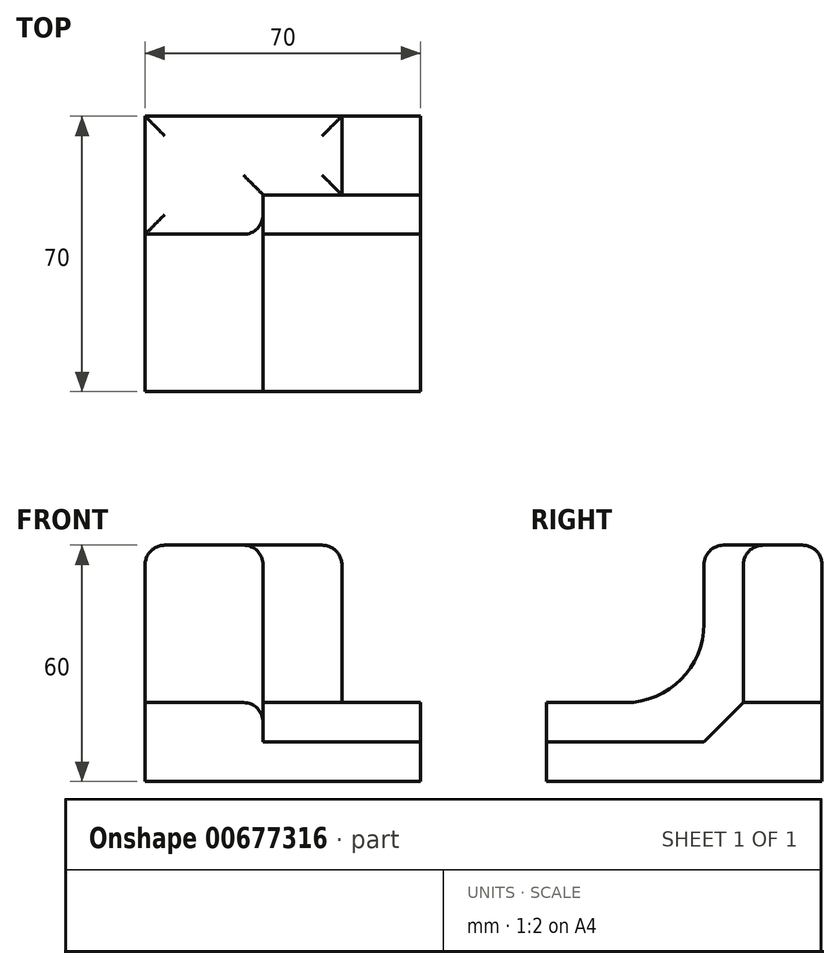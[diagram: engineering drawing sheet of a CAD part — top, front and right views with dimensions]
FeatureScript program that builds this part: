
annotation { "Feature Type Name" : "Feature", "Feature Type Description" : "" }
export const myFeature = defineFeature(function(context is Context, id is Id, definition is map)
    precondition{}
    {
        {
            var Q0;
            Q0=qCreatedBy(makeId("Top.planeOp"),FACE);
            var sketch = newSketch(context, id + "F0", { "sketchPlane" : qUnion([Q0])});
            skLineSegment(sketch, "E0.bottom", {"start": v(0, 0) * mm, "end": v(70, 0) * mm});
            skLineSegment(sketch, "E0.top", {"start": v(0, 70) * mm, "end": v(70, 70) * mm});
            skLineSegment(sketch, "E0.left", {"start": v(0, 0) * mm, "end": v(0, 70) * mm});
            skLineSegment(sketch, "E0.right", {"start": v(70, 0) * mm, "end": v(70, 70) * mm});
            skSolve(sketch);
        }
        {
            var Q0;
            Q0 = qSketchRegion(id + "F0", true);
            extrude(context, id + "F1", {"entities" : qUnion([Q0]), "depth" : 60 * mm, "offsetDistance" : 25 * mm});
        }
        {
            var Q0;
            Q0=makeQuery(id+"F1.opExtrude","SWEPT_FACE",FACE,{"disambiguationData":[OSD([sQuery(id+"F0.wireOp",EDGE,"E0.right")])]});
            var sketch = newSketch(context, id + "F2", { "sketchPlane" : qUnion([Q0])});
            skLineSegment(sketch, "E1", {"start": v(0, 60) * mm, "end": v(40, 60) * mm});
            skLineSegment(sketch, "E2", {"start": v(40, 60) * mm, "end": v(40, 40) * mm});
            skLineSegment(sketch, "E3", {"start": v(20, 20) * mm, "end": v(0, 20) * mm});
            skLineSegment(sketch, "E4", {"start": v(0, 20) * mm, "end": v(0, 60) * mm});
            skPoint(sketch, "E5.visualSharp", {"position": v(40, 20) * mm});
            skArc(sketch, "E5.filletArc", {"start": v(20, 20) * mm, "mid": v(34.14, 25.86) * mm, "end": v(40, 40) * mm});
            skSolve(sketch);
        }
        {
            var Q0;
            Q0 = qSketchRegion(id + "F2", true);
            extrude(context, id + "F3", {"entities" : qUnion([Q0]), "operationType" : NewBodyOperationType.REMOVE, "endBound" : BoundingType.THROUGH_ALL, "oppositeDirection" : true, "depth" : 25 * mm, "offsetDistance" : 25 * mm});
        }
        {
            var Q0;
            Q0=makeQuery(id+"F1.opExtrude","SWEPT_FACE",FACE,{"disambiguationData":[OSD([sQuery(id+"F0.wireOp",EDGE,"E0.right")])]});
            var sketch = newSketch(context, id + "F4", { "sketchPlane" : qUnion([Q0])});
            skLineSegment(sketch, "E6", {"start": v(0, 10) * mm, "end": v(50, 10) * mm});
            skLineSegment(sketch, "E7", {"start": v(50, 10) * mm, "end": v(50, 60) * mm});
            skLineSegment(sketch, "E8", {"start": v(0, 10) * mm, "end": v(0, 60) * mm});
            skLineSegment(sketch, "E9", {"start": v(0, 60) * mm, "end": v(50, 60) * mm});
            skPoint(sketch, "E10.visualSharp", {"position": v(50, 10) * mm});
            skSolve(sketch);
        }
        {
            var Q0;
            Q0 = qSketchRegion(id + "F4", true);
            extrude(context, id + "F5", {"entities" : qUnion([Q0]), "operationType" : NewBodyOperationType.REMOVE, "oppositeDirection" : true, "depth" : 40 * mm, "offsetDistance" : 25 * mm});
        }
        {
            var Q0;
            Q0=makeQuery(id+"F5.boolean.opBoolean","COPY",EDGE,{"derivedFrom":makeQuery(id+"F5.opExtrude","SWEPT_EDGE",EDGE,{"disambiguationData":[OSD([sQuery(id+"F4.wireOp",EDGE,"E6"),sQuery(id+"F4.wireOp",EDGE,"E7")])]})});
            chamfer(context, id + "F6", {"entities" : qUnion([Q0]), "width" : 10 * mm, "tangentPropagation" : true});
        }
        {
            var Q0;
            Q0=makeQuery(id+"F1.opExtrude","SWEPT_FACE",FACE,{"disambiguationData":[OSD([sQuery(id+"F0.wireOp",EDGE,"E0.right")])]});
            var sketch = newSketch(context, id + "F7", { "sketchPlane" : qUnion([Q0])});
            skLineSegment(sketch, "E11.bottom", {"start": v(50, 20) * mm, "end": v(70, 20) * mm});
            skLineSegment(sketch, "E11.top", {"start": v(50, 60) * mm, "end": v(70, 60) * mm});
            skLineSegment(sketch, "E11.left", {"start": v(50, 20) * mm, "end": v(50, 60) * mm});
            skLineSegment(sketch, "E11.right", {"start": v(70, 20) * mm, "end": v(70, 60) * mm});
            skSolve(sketch);
        }
        {
            var Q0;
            Q0 = qSketchRegion(id + "F7", true);
            extrude(context, id + "F8", {"entities" : qUnion([Q0]), "operationType" : NewBodyOperationType.REMOVE, "oppositeDirection" : true, "depth" : 20 * mm, "offsetDistance" : 25 * mm});
        }
        {
            var Q0;
            Q0=makeQuery(id+"F1.opExtrude","CAP_FACE",FACE,{"disambiguationData":[OSD([sQuery(id+"F0.wireOp",EDGE,"E0.bottom"),sQuery(id+"F0.wireOp",EDGE,"E0.top"),sQuery(id+"F0.wireOp",EDGE,"E0.left"),sQuery(id+"F0.wireOp",EDGE,"E0.right")])],"isStart":false});
            fillet(context, id + "F9", {"entities" : qUnion([Q0]), "radius" : 5 * mm, "tangentPropagation" : true, "allowEdgeOverflow" : false});
        }
        {
            var Q0;
            Q0=makeQuery(id+"F5.boolean.opBoolean","INTERSECT",EDGE,{"derivedFrom":[makeQuery(id+"F3.boolean.opBoolean","COPY",FACE,{"derivedFrom":makeQuery(id+"F3.opExtrude","SWEPT_FACE",FACE,{"disambiguationData":[OSD([sQuery(id+"F2.wireOp",EDGE,"E3")])]})}),makeQuery(id+"F5.opExtrude","CAP_FACE",FACE,{"disambiguationData":[OSD([sQuery(id+"F4.wireOp",EDGE,"E6"),sQuery(id+"F4.wireOp",EDGE,"E7"),sQuery(id+"F4.wireOp",EDGE,"E8"),sQuery(id+"F4.wireOp",EDGE,"E9")])],"isStart":false})]});
            fillet(context, id + "F10", {"entities" : qUnion([Q0]), "radius" : 5 * mm, "tangentPropagation" : true, "allowEdgeOverflow" : false});
        }
    });
